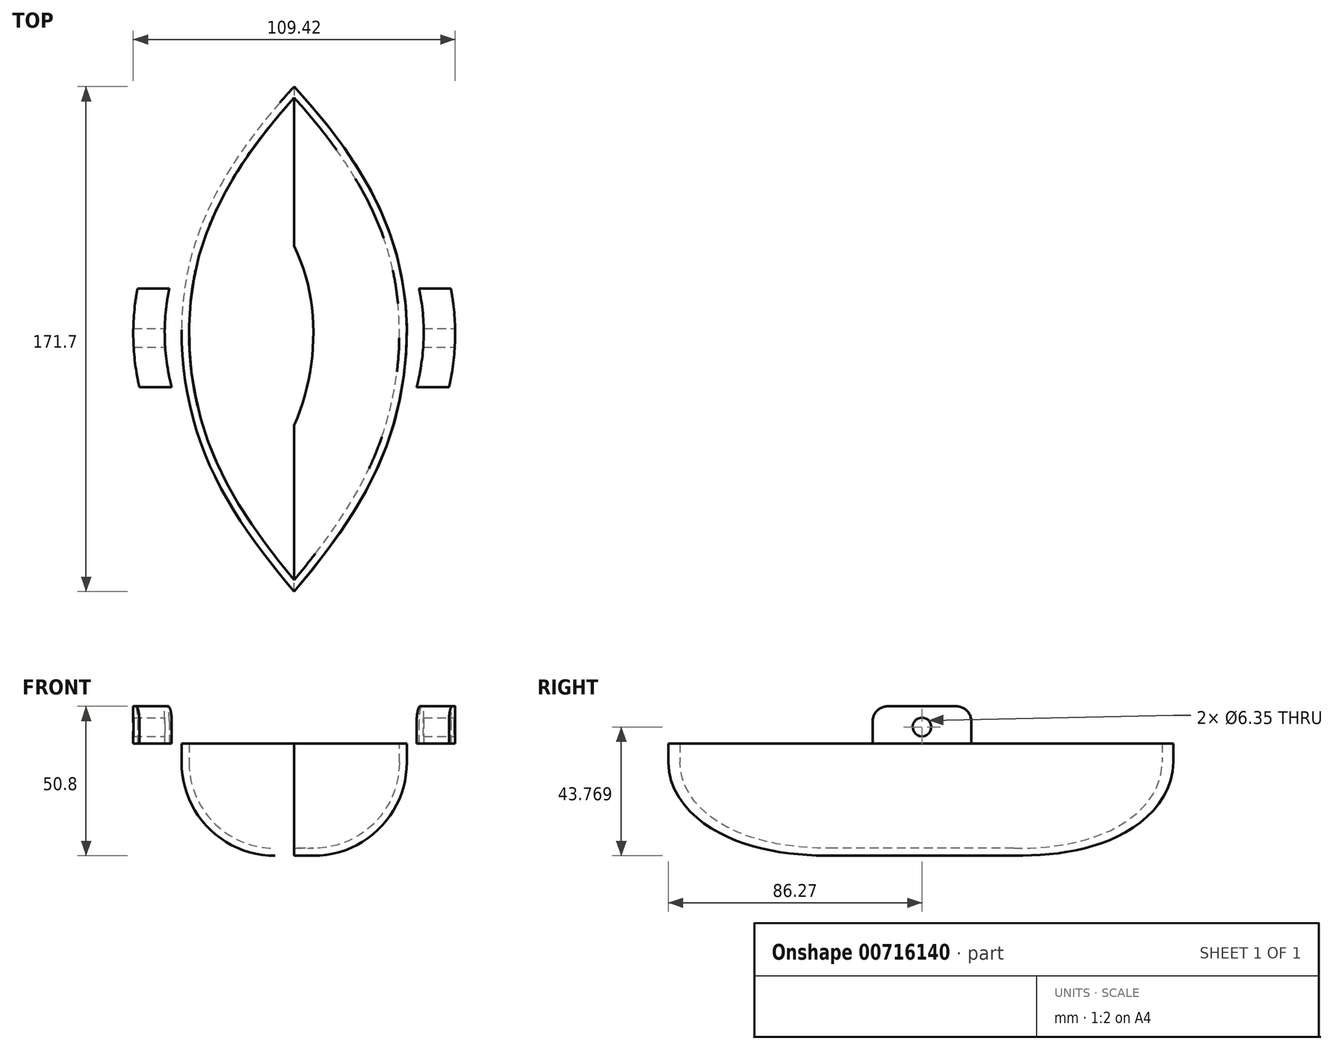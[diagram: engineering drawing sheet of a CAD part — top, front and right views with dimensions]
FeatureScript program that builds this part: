
annotation { "Feature Type Name" : "Feature", "Feature Type Description" : "" }
export const myFeature = defineFeature(function(context is Context, id is Id, definition is map)
    precondition{}
    {
        {
            var Q0;
            Q0=qCreatedBy(makeId("Top.planeOp"),FACE);
            var sketch = newSketch(context, id + "F0", { "sketchPlane" : qUnion([Q0])});
            skLineSegment(sketch, "E0", {"start": v(0, 96.37) * mm, "end": v(0, -97.21) * mm, "construction": true});
            skFitSpline(sketch, "E1", {"points": [v(0, 85.43) * mm, v(-34.93, 27.99) * mm, v(-33.25, -31.35) * mm, v(0, -86.27) * mm], "startDerivative": vector(-145.18, -157.6) * mm, "endDerivative": vector(144.38, -171.52) * mm});
            skFitSpline(sketch, "E2.MirrorCS", {"points": [v(0, 85.43) * mm, v(34.93, 27.99) * mm, v(33.25, -31.35) * mm, v(0, -86.27) * mm], "startDerivative": vector(145.18, -157.6) * mm, "endDerivative": vector(-144.38, -171.52) * mm});
            skSolve(sketch);
        }
        {
            var Q0;
            Q0 = qSketchRegion(id + "F0", true);
            extrude(context, id + "F1", {"entities" : qUnion([Q0]), "depth" : 38.1 * mm, "offsetDistance" : 25.4 * mm});
        }
        {
            var Q0;
            Q0=makeQuery(id+"F1.opExtrude","CAP_EDGE",EDGE,{"disambiguationData":[OSD([sQuery(id+"F0.wireOp",EDGE,"E2.MirrorCS")])],"isStart":true});
            var Q1;
            Q1=makeQuery(id+"F1.opExtrude","CAP_EDGE",EDGE,{"disambiguationData":[OSD([sQuery(id+"F0.wireOp",EDGE,"E1")])],"isStart":true});
            fillet(context, id + "F2", {"entities" : qUnion([Q0, Q1]), "radius" : 31.75 * mm, "tangentPropagation" : true, "allowEdgeOverflow" : false});
        }
        {
            var Q0;
            Q0=makeQuery(id+"F1.opExtrude","CAP_FACE",FACE,{"disambiguationData":[OSD([sQuery(id+"F0.wireOp",EDGE,"E1"),sQuery(id+"F0.wireOp",EDGE,"E2.MirrorCS")])],"isStart":false});
            shell(context, id + "F3", {"entities" : qUnion([Q0]), "thickness" : 2.54 * mm});
        }
        {
            var Q0;
            Q0=qCreatedBy(makeId("Right.planeOp"),FACE);
            cPlane(context, id + "F4", {"entities" : qUnion([Q0]), "cplaneType" : CPlaneType.OFFSET, "offset" : 76.2 * mm, "width" : 152.4 * mm, "height" : 152.4 * mm});
        }
        {
            var Q0;
            Q0=makeQuery(id+"F1.opExtrude","SWEPT_BODY",BODY,{"disambiguationData":[OSD([sQuery(id+"F0.wireOp",EDGE,"E1"),sQuery(id+"F0.wireOp",EDGE,"E2.MirrorCS")])]});
            var Q1;
            Q1=qCreatedBy(id+"F4.planeOp",FACE);
            mirror(context, id + "F5", {"entities" : qUnion([Q0]), "mirrorPlane" : qUnion([Q1])});
        }
        {
            var Q0;
            Q0=makeQuery(id+"F5.opPattern","COPY",FACE,{"derivedFrom":makeQuery(id+"F1.opExtrude","CAP_FACE",FACE,{"disambiguationData":[OSD([sQuery(id+"F0.wireOp",EDGE,"E1"),sQuery(id+"F0.wireOp",EDGE,"E2.MirrorCS")])],"isStart":false}),"instanceName":"1"});
            var sketch = newSketch(context, id + "F6", { "sketchPlane" : qUnion([Q0])});
            skFitSpline(sketch, "E3.0", {"points": [v(152.4, 81.68) * mm, v(149.7, 78.76) * mm, v(144.33, 72.9) * mm, v(137.77, 65.44) * mm, v(132.7, 59.32) * mm, v(129.01, 54.64) * mm, v(126.06, 50.63) * mm, v(123.8, 47.35) * mm, v(121.6, 44.04) * mm, v(119.01, 39.81) * mm, v(116.2, 34.59) * mm, v(114.15, 30.08) * mm, v(112.72, 26.38) * mm, v(111.91, 24.01) * mm, v(111.33, 22.1) * mm, v(110.78, 20.17) * mm, v(110.17, 17.76) * mm, v(109.57, 14.85) * mm, v(109.08, 11.93) * mm, v(108.72, 8.98) * mm, v(108.48, 6.02) * mm, v(108.37, 3.04) * mm, v(108.38, 0.55) * mm, v(108.45, -1.46) * mm, v(108.56, -3.45) * mm, v(108.78, -5.93) * mm, v(109.16, -8.88) * mm, v(109.83, -12.79) * mm, v(110.73, -16.65) * mm, v(111.85, -20.46) * mm, v(112.8, -23.3) * mm, v(113.87, -26.1) * mm, v(115.02, -28.86) * mm, v(116.26, -31.57) * mm, v(118, -35.12) * mm, v(120.36, -39.46) * mm, v(124.44, -46.23) * mm, v(128.9, -52.78) * mm, v(133.63, -59.18) * mm, v(138.48, -65.47) * mm, v(144.73, -73.2) * mm, v(149.84, -79.29) * mm, v(152.4, -82.33) * mm]});
            skFitSpline(sketch, "E3.1", {"points": [v(152.4, 85.43) * mm, v(135.86, 67.48) * mm, v(104.67, 33.62) * mm, v(103.61, -28.32) * mm, v(135.3, -65.96) * mm, v(152.4, -86.27) * mm]});
            skFitSpline(sketch, "E3.2", {"points": [v(152.4, 81.68) * mm, v(155.1, 78.76) * mm, v(160.47, 72.9) * mm, v(167.03, 65.44) * mm, v(172.1, 59.32) * mm, v(175.79, 54.64) * mm, v(178.74, 50.63) * mm, v(181, 47.35) * mm, v(183.2, 44.04) * mm, v(185.79, 39.81) * mm, v(188.6, 34.59) * mm, v(190.65, 30.08) * mm, v(192.08, 26.38) * mm, v(192.89, 24.01) * mm, v(193.47, 22.1) * mm, v(194.02, 20.17) * mm, v(194.63, 17.76) * mm, v(195.23, 14.85) * mm, v(195.72, 11.93) * mm, v(196.08, 8.98) * mm, v(196.32, 6.02) * mm, v(196.43, 3.04) * mm, v(196.42, 0.55) * mm, v(196.35, -1.46) * mm, v(196.24, -3.45) * mm, v(196.02, -5.93) * mm, v(195.64, -8.88) * mm, v(194.97, -12.79) * mm, v(194.07, -16.65) * mm, v(192.95, -20.46) * mm, v(192, -23.3) * mm, v(190.93, -26.1) * mm, v(189.78, -28.86) * mm, v(188.54, -31.57) * mm, v(186.8, -35.12) * mm, v(184.44, -39.46) * mm, v(180.36, -46.23) * mm, v(175.9, -52.78) * mm, v(171.17, -59.18) * mm, v(166.32, -65.47) * mm, v(160.07, -73.2) * mm, v(154.96, -79.29) * mm, v(152.4, -82.33) * mm]});
            skFitSpline(sketch, "E3.3", {"points": [v(152.4, 85.43) * mm, v(168.94, 67.48) * mm, v(200.13, 33.62) * mm, v(201.19, -28.32) * mm, v(169.5, -65.96) * mm, v(152.4, -86.27) * mm]});
            skSolve(sketch);
        }
        {
            var Q0;
            Q0 = qSketchRegion(id + "F6", true);
            extrude(context, id + "F7", {"entities" : qUnion([Q0]), "operationType" : NewBodyOperationType.ADD, "depth" : 12.7 * mm, "offsetDistance" : 25.4 * mm});
        }
        {
            var Q0;
            Q0=makeQuery(id+"F7.opExtrude","CAP_FACE",FACE,{"disambiguationData":[OSD([sQuery(id+"F6.wireOp",EDGE,"E3.0"),sQuery(id+"F6.wireOp",EDGE,"E3.1"),sQuery(id+"F6.wireOp",EDGE,"E3.2"),sQuery(id+"F6.wireOp",EDGE,"E3.3")])],"isStart":false});
            cPlane(context, id + "F8", {"entities" : qUnion([Q0]), "cplaneType" : CPlaneType.OFFSET, "offset" : 25.4 * mm, "width" : 152.4 * mm, "height" : 152.4 * mm});
        }
        {
            var Q0;
            Q0=qCreatedBy(id+"F8.planeOp",FACE);
            var sketch = newSketch(context, id + "F9", { "sketchPlane" : qUnion([Q0])});
            skLineSegment(sketch, "E4.bottom", {"start": v(219.78, -16.76) * mm, "end": v(78.18, -16.76) * mm});
            skLineSegment(sketch, "E4.top", {"start": v(219.78, 16.76) * mm, "end": v(78.18, 16.76) * mm});
            skLineSegment(sketch, "E4.left", {"start": v(219.78, -16.76) * mm, "end": v(219.78, 16.76) * mm});
            skLineSegment(sketch, "E4.right", {"start": v(78.18, -16.76) * mm, "end": v(78.18, 16.76) * mm});
            skPoint(sketch, "E4.middle", {"position": v(148.98, 0) * mm});
            skSolve(sketch);
        }
        {
            var Q0;
            Q0=makeQuery(id+"F9.imprint","IMPRINT",FACE,{"disambiguationData":[TD([[makeQuery(id+"F9.imprint","IMPRINT",EDGE,{"derivedFrom":sQuery(id+"F9.wireOp",EDGE,"E4.bottom")}),-1.0]])]});
            extrude(context, id + "F10", {"entities" : qUnion([Q0]), "oppositeDirection" : true, "depth" : 38.1 * mm, "offsetDistance" : 25.4 * mm});
        }
        {
            var Q0;
            Q0=makeQuery(id+"F5.opPattern","COPY",BODY,{"derivedFrom":makeQuery(id+"F1.opExtrude","SWEPT_BODY",BODY,{"disambiguationData":[OSD([sQuery(id+"F0.wireOp",EDGE,"E1"),sQuery(id+"F0.wireOp",EDGE,"E2.MirrorCS")])]}),"instanceName":"1"});
            var Q1;
            Q1=makeQuery(id+"F10.opExtrude","SWEPT_BODY",BODY,{"disambiguationData":[OSD([sQuery(id+"F9.wireOp",EDGE,"E4.bottom"),sQuery(id+"F9.wireOp",EDGE,"E4.top"),sQuery(id+"F9.wireOp",EDGE,"E4.left"),sQuery(id+"F9.wireOp",EDGE,"E4.right")])]});
            booleanBodies(context, id + "F11", {"operationType" : BooleanOperationType.INTERSECTION, "tools" : qUnion([Q0, Q1])});
        }
        {
            var Q0;
            Q0=makeQuery(id+"F11.opBoolean","INTERSECT",BODY,{"disambiguationData":[OD(1.0)],"derivedFrom":[makeQuery(id+"F5.opPattern","COPY",BODY,{"derivedFrom":makeQuery(id+"F1.opExtrude","SWEPT_BODY",BODY,{"disambiguationData":[OSD([sQuery(id+"F0.wireOp",EDGE,"E1"),sQuery(id+"F0.wireOp",EDGE,"E2.MirrorCS")])]}),"instanceName":"1"}),makeQuery(id+"F10.opExtrude","SWEPT_BODY",BODY,{"disambiguationData":[OSD([sQuery(id+"F9.wireOp",EDGE,"E4.bottom"),sQuery(id+"F9.wireOp",EDGE,"E4.top"),sQuery(id+"F9.wireOp",EDGE,"E4.left"),sQuery(id+"F9.wireOp",EDGE,"E4.right")])]})]});
            var Q1;
            Q1=makeQuery(id+"F11.opBoolean","INTERSECT",BODY,{"disambiguationData":[OD(0.0)],"derivedFrom":[makeQuery(id+"F5.opPattern","COPY",BODY,{"derivedFrom":makeQuery(id+"F1.opExtrude","SWEPT_BODY",BODY,{"disambiguationData":[OSD([sQuery(id+"F0.wireOp",EDGE,"E1"),sQuery(id+"F0.wireOp",EDGE,"E2.MirrorCS")])]}),"instanceName":"1"}),makeQuery(id+"F10.opExtrude","SWEPT_BODY",BODY,{"disambiguationData":[OSD([sQuery(id+"F9.wireOp",EDGE,"E4.bottom"),sQuery(id+"F9.wireOp",EDGE,"E4.top"),sQuery(id+"F9.wireOp",EDGE,"E4.left"),sQuery(id+"F9.wireOp",EDGE,"E4.right")])]})]});
            var Q2;
            Q2=qCreatedBy(id+"F4.planeOp",FACE);
            mirror(context, id + "F12", {"operationType" : NewBodyOperationType.ADD, "entities" : qUnion([Q0, Q1]), "mirrorPlane" : qUnion([Q2])});
        }
        {
            var Q0;
            Q0=makeQuery(id+"F11.opBoolean","INTERSECT",BODY,{"disambiguationData":[OD(0.0)],"derivedFrom":[makeQuery(id+"F5.opPattern","COPY",BODY,{"derivedFrom":makeQuery(id+"F1.opExtrude","SWEPT_BODY",BODY,{"disambiguationData":[OSD([sQuery(id+"F0.wireOp",EDGE,"E1"),sQuery(id+"F0.wireOp",EDGE,"E2.MirrorCS")])]}),"instanceName":"1"}),makeQuery(id+"F10.opExtrude","SWEPT_BODY",BODY,{"disambiguationData":[OSD([sQuery(id+"F9.wireOp",EDGE,"E4.bottom"),sQuery(id+"F9.wireOp",EDGE,"E4.top"),sQuery(id+"F9.wireOp",EDGE,"E4.left"),sQuery(id+"F9.wireOp",EDGE,"E4.right")])]})]});
            var Q1;
            Q1=makeQuery(id+"F11.opBoolean","INTERSECT",BODY,{"disambiguationData":[OD(1.0)],"derivedFrom":[makeQuery(id+"F5.opPattern","COPY",BODY,{"derivedFrom":makeQuery(id+"F1.opExtrude","SWEPT_BODY",BODY,{"disambiguationData":[OSD([sQuery(id+"F0.wireOp",EDGE,"E1"),sQuery(id+"F0.wireOp",EDGE,"E2.MirrorCS")])]}),"instanceName":"1"}),makeQuery(id+"F10.opExtrude","SWEPT_BODY",BODY,{"disambiguationData":[OSD([sQuery(id+"F9.wireOp",EDGE,"E4.bottom"),sQuery(id+"F9.wireOp",EDGE,"E4.top"),sQuery(id+"F9.wireOp",EDGE,"E4.left"),sQuery(id+"F9.wireOp",EDGE,"E4.right")])]})]});
            deleteBodies(context, id + "F13", {"entities" : qUnion([Q0, Q1])});
        }
        {
            var Q0;
            Q0=qCreatedBy(makeId("Right.planeOp"),FACE);
            var sketch = newSketch(context, id + "F14", { "sketchPlane" : qUnion([Q0])});
            skCircle(sketch, "E5", {"center": v(0, 43.77) * mm, "radius": 3.18 * mm});
            skSolve(sketch);
        }
        {
            var Q0;
            Q0 = qSketchRegion(id + "F14", true);
            extrude(context, id + "F15", {"entities" : qUnion([Q0]), "operationType" : NewBodyOperationType.REMOVE, "endBound" : BoundingType.THROUGH_ALL, "oppositeDirection" : true, "depth" : 25.4 * mm, "offsetDistance" : 25.4 * mm, "hasSecondDirection" : true, "secondDirectionBound" : SecondDirectionBoundingType.THROUGH_ALL, "secondDirectionOppositeDirection" : false, "secondDirectionDepth" : 25.4 * mm});
        }
        {
            var Q0;
            Q0=makeQuery(id+"F12.opPattern","COPY",EDGE,{"derivedFrom":makeQuery(id+"F11.opBoolean","INTERSECT",EDGE,{"disambiguationData":[OD(0.0)],"derivedFrom":[makeQuery(id+"F7.opExtrude","CAP_FACE",FACE,{"disambiguationData":[OSD([sQuery(id+"F6.wireOp",EDGE,"E3.0"),sQuery(id+"F6.wireOp",EDGE,"E3.1"),sQuery(id+"F6.wireOp",EDGE,"E3.2"),sQuery(id+"F6.wireOp",EDGE,"E3.3")])],"isStart":false}),makeQuery(id+"F10.opExtrude","SWEPT_FACE",FACE,{"disambiguationData":[OSD([sQuery(id+"F9.wireOp",EDGE,"E4.top")])]})]}),"instanceName":"1"});
            var Q1;
            Q1=makeQuery(id+"F12.opPattern","COPY",EDGE,{"derivedFrom":makeQuery(id+"F11.opBoolean","INTERSECT",EDGE,{"disambiguationData":[OD(0.0)],"derivedFrom":[makeQuery(id+"F7.opExtrude","CAP_FACE",FACE,{"disambiguationData":[OSD([sQuery(id+"F6.wireOp",EDGE,"E3.0"),sQuery(id+"F6.wireOp",EDGE,"E3.1"),sQuery(id+"F6.wireOp",EDGE,"E3.2"),sQuery(id+"F6.wireOp",EDGE,"E3.3")])],"isStart":false}),makeQuery(id+"F10.opExtrude","SWEPT_FACE",FACE,{"disambiguationData":[OSD([sQuery(id+"F9.wireOp",EDGE,"E4.bottom")])]})]}),"instanceName":"1"});
            var Q2;
            Q2=makeQuery(id+"F12.opPattern","COPY",EDGE,{"derivedFrom":makeQuery(id+"F11.opBoolean","INTERSECT",EDGE,{"disambiguationData":[OD(1.0)],"derivedFrom":[makeQuery(id+"F7.opExtrude","CAP_FACE",FACE,{"disambiguationData":[OSD([sQuery(id+"F6.wireOp",EDGE,"E3.0"),sQuery(id+"F6.wireOp",EDGE,"E3.1"),sQuery(id+"F6.wireOp",EDGE,"E3.2"),sQuery(id+"F6.wireOp",EDGE,"E3.3")])],"isStart":false}),makeQuery(id+"F10.opExtrude","SWEPT_FACE",FACE,{"disambiguationData":[OSD([sQuery(id+"F9.wireOp",EDGE,"E4.top")])]})]}),"instanceName":"1"});
            var Q3;
            Q3=makeQuery(id+"F12.opPattern","COPY",EDGE,{"derivedFrom":makeQuery(id+"F11.opBoolean","INTERSECT",EDGE,{"disambiguationData":[OD(1.0)],"derivedFrom":[makeQuery(id+"F7.opExtrude","CAP_FACE",FACE,{"disambiguationData":[OSD([sQuery(id+"F6.wireOp",EDGE,"E3.0"),sQuery(id+"F6.wireOp",EDGE,"E3.1"),sQuery(id+"F6.wireOp",EDGE,"E3.2"),sQuery(id+"F6.wireOp",EDGE,"E3.3")])],"isStart":false}),makeQuery(id+"F10.opExtrude","SWEPT_FACE",FACE,{"disambiguationData":[OSD([sQuery(id+"F9.wireOp",EDGE,"E4.bottom")])]})]}),"instanceName":"1"});
            var Q4;
            {var subQ0=sQuery(id+"F9.wireOp",EDGE,"E4.top");Q4=makeQuery(id+"F12.opPattern","COPY",EDGE,{"derivedFrom":makeQuery(id+"F11.opBoolean","SPLIT",EDGE,{"disambiguationData":[TD([makeQuery(id+"F5.opPattern","COPY",FACE,{"derivedFrom":makeQuery(id+"F1.opExtrude","SWEPT_FACE",FACE,{"disambiguationData":[OSD([sQuery(id+"F0.wireOp",EDGE,"E1")])]}),"instanceName":"1"})])],"derivedFrom":makeQuery(id+"F10.opExtrude","CAP_EDGE",EDGE,{"disambiguationData":[OSD([subQ0])],"isStart":false})}),"instanceName":"1"});}
            var Q5;
            {var subQ0=sQuery(id+"F9.wireOp",EDGE,"E4.bottom");Q5=makeQuery(id+"F12.opPattern","COPY",EDGE,{"derivedFrom":makeQuery(id+"F11.opBoolean","SPLIT",EDGE,{"disambiguationData":[TD([makeQuery(id+"F5.opPattern","COPY",FACE,{"derivedFrom":makeQuery(id+"F1.opExtrude","SWEPT_FACE",FACE,{"disambiguationData":[OSD([sQuery(id+"F0.wireOp",EDGE,"E1")])]}),"instanceName":"1"})])],"derivedFrom":makeQuery(id+"F10.opExtrude","CAP_EDGE",EDGE,{"disambiguationData":[OSD([subQ0])],"isStart":false})}),"instanceName":"1"});}
            var Q6;
            {var subQ0=sQuery(id+"F9.wireOp",EDGE,"E4.bottom");Q6=makeQuery(id+"F12.opPattern","COPY",EDGE,{"derivedFrom":makeQuery(id+"F11.opBoolean","SPLIT",EDGE,{"disambiguationData":[TD([makeQuery(id+"F5.opPattern","COPY",FACE,{"derivedFrom":makeQuery(id+"F1.opExtrude","SWEPT_FACE",FACE,{"disambiguationData":[OSD([sQuery(id+"F0.wireOp",EDGE,"E2.MirrorCS")])]}),"instanceName":"1"})])],"derivedFrom":makeQuery(id+"F10.opExtrude","CAP_EDGE",EDGE,{"disambiguationData":[OSD([subQ0])],"isStart":false})}),"instanceName":"1"});}
            var Q7;
            {var subQ0=sQuery(id+"F9.wireOp",EDGE,"E4.top");Q7=makeQuery(id+"F12.opPattern","COPY",EDGE,{"derivedFrom":makeQuery(id+"F11.opBoolean","SPLIT",EDGE,{"disambiguationData":[TD([makeQuery(id+"F5.opPattern","COPY",FACE,{"derivedFrom":makeQuery(id+"F1.opExtrude","SWEPT_FACE",FACE,{"disambiguationData":[OSD([sQuery(id+"F0.wireOp",EDGE,"E2.MirrorCS")])]}),"instanceName":"1"})])],"derivedFrom":makeQuery(id+"F10.opExtrude","CAP_EDGE",EDGE,{"disambiguationData":[OSD([subQ0])],"isStart":false})}),"instanceName":"1"});}
            fillet(context, id + "F16", {"entities" : qUnion([Q0, Q1, Q2, Q3, Q4, Q5, Q6, Q7]), "radius" : 5.08 * mm, "tangentPropagation" : true, "allowEdgeOverflow" : false});
        }
    });
